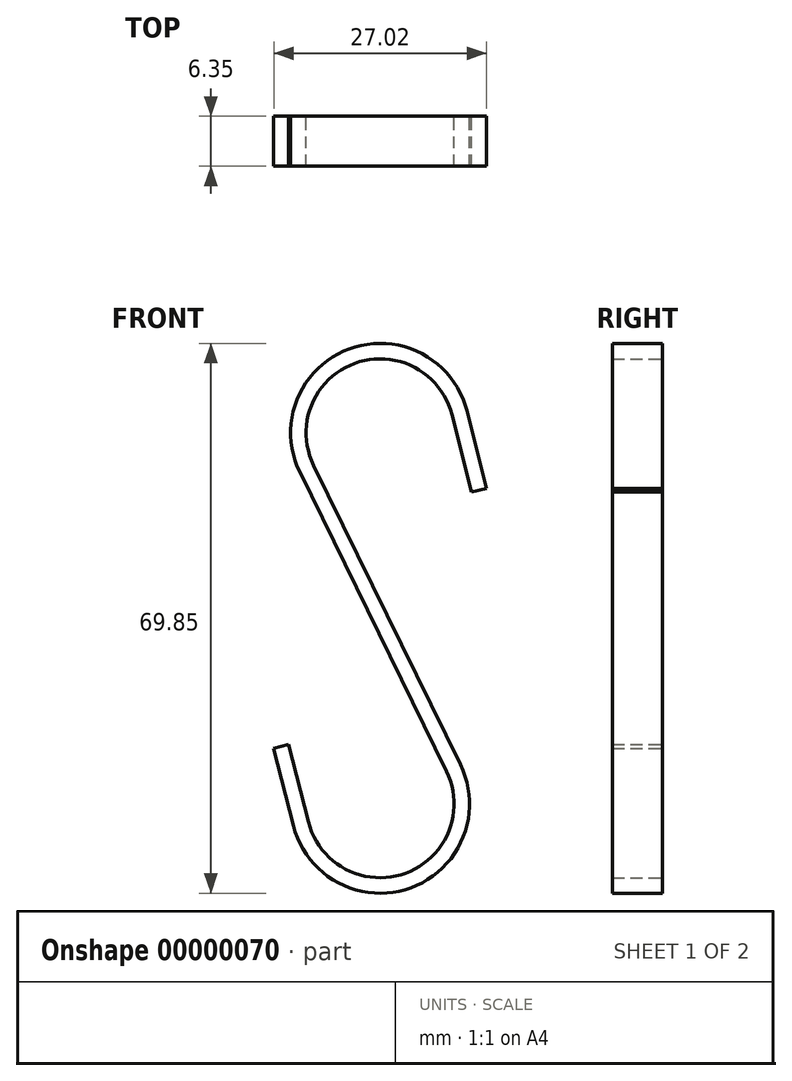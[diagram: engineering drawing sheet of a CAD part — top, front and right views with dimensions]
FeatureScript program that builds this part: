
annotation { "Feature Type Name" : "Feature", "Feature Type Description" : "" }
export const myFeature = defineFeature(function(context is Context, id is Id, definition is map)
    precondition{}
    {
        {
            var Q0;
            Q0=qCreatedBy(makeId("Front.planeOp"),FACE);
            var sketch = newSketch(context, id + "F0", { "sketchPlane" : qUnion([Q0])});
            skCircle(sketch, "E0", {"center": v(0, 0) * mm, "radius": 8.13 * mm, "construction": true});
            skArc(sketch, "E1", {"start": v(9.1, 2.32) * mm, "mid": v(-3.25, 8.82) * mm, "end": v(-8.44, -4.14) * mm});
            skArc(sketch, "E2", {"start": v(-11, -49.93) * mm, "mid": v(3.92, -57.8) * mm, "end": v(10.2, -42.13) * mm});
            skArc(sketch, "E3.0", {"start": v(-9.1, -49.45) * mm, "mid": v(3.25, -55.95) * mm, "end": v(8.44, -43) * mm});
            skArc(sketch, "E3.1", {"start": v(11, 2.8) * mm, "mid": v(-3.92, 10.66) * mm, "end": v(-10.2, -5) * mm});
            skLineSegment(sketch, "E4", {"start": v(-11, -49.93) * mm, "end": v(-9.1, -49.45) * mm});
            skLineSegment(sketch, "E5", {"start": v(11, 2.8) * mm, "end": v(9.1, 2.32) * mm});
            skLineSegment(sketch, "E6", {"start": v(-10.2, -5) * mm, "end": v(8.44, -43) * mm});
            skLineSegment(sketch, "E7", {"start": v(-8.44, -4.14) * mm, "end": v(10.2, -42.13) * mm});
            skLineSegment(sketch, "E8", {"start": v(0.88, -23.13) * mm, "end": v(-0.88, -24) * mm, "construction": true});
            skPoint(sketch, "E9", {"position": v(0, -23.57) * mm});
            skLineSegment(sketch, "E10", {"start": v(-9.1, -49.45) * mm, "end": v(7.59, -41.26) * mm, "construction": true});
            skLineSegment(sketch, "E11", {"start": v(9.1, 2.32) * mm, "end": v(-7.59, -5.87) * mm, "construction": true});
            skLineSegment(sketch, "E12", {"start": v(9.1, 2.32) * mm, "end": v(11.61, -7.53) * mm});
            skLineSegment(sketch, "E13", {"start": v(11.61, -7.53) * mm, "end": v(13.51, -7.04) * mm});
            skLineSegment(sketch, "E14", {"start": v(13.51, -7.04) * mm, "end": v(11, 2.8) * mm});
            skLineSegment(sketch, "E15", {"start": v(-11, -49.93) * mm, "end": v(-13.51, -40.09) * mm});
            skLineSegment(sketch, "E16", {"start": v(-13.51, -40.09) * mm, "end": v(-11.61, -39.6) * mm});
            skLineSegment(sketch, "E17", {"start": v(-11.61, -39.6) * mm, "end": v(-9.1, -49.45) * mm});
            skLineSegment(sketch, "E18", {"start": v(11.61, -7.53) * mm, "end": v(-3.2, -14.8) * mm, "construction": true});
            skSolve(sketch);
        }
        {
            var Q0;
            Q0=makeQuery(id+"F0.imprint","IMPRINT",FACE,{"disambiguationData":[TD([[makeQuery(id+"F0.imprint","IMPRINT",EDGE,{"derivedFrom":sQuery(id+"F0.wireOp",EDGE,"E1")}),-1.0]])]});
            var Q1;
            Q1=makeQuery(id+"F0.imprint","IMPRINT",FACE,{"disambiguationData":[TD([[makeQuery(id+"F0.imprint","IMPRINT",EDGE,{"derivedFrom":sQuery(id+"F0.wireOp",EDGE,"E5")}),1.0]])]});
            var Q2;
            Q2=makeQuery(id+"F0.imprint","IMPRINT",FACE,{"disambiguationData":[TD([[makeQuery(id+"F0.imprint","IMPRINT",EDGE,{"derivedFrom":sQuery(id+"F0.wireOp",EDGE,"E4")}),1.0]])]});
            extrude(context, id + "F1", {"entities" : qUnion([Q0, Q1, Q2]), "depth" : 6.35 * mm});
        }
    });
